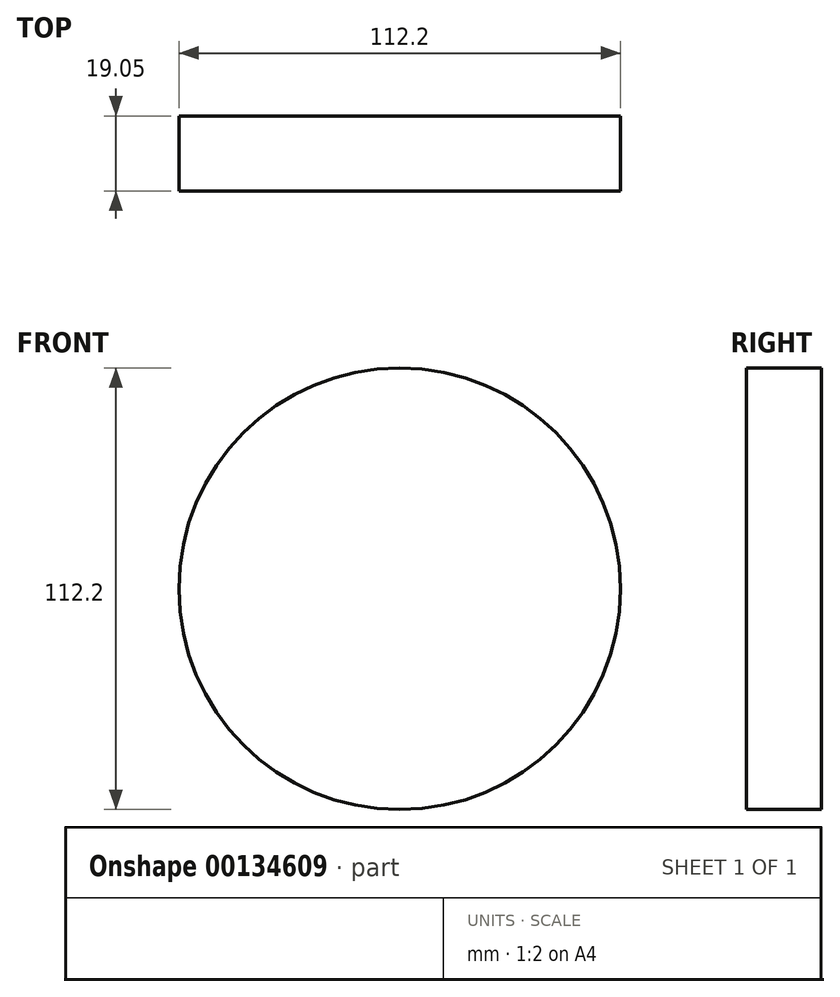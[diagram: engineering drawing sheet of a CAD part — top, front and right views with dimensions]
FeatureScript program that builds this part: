
annotation { "Feature Type Name" : "Feature", "Feature Type Description" : "" }
export const myFeature = defineFeature(function(context is Context, id is Id, definition is map)
    precondition{}
    {
        {
            var Q0;
            Q0=qCreatedBy(makeId("Front.planeOp"),FACE);
            var sketch = newSketch(context, id + "F0", { "sketchPlane" : qUnion([Q0])});
            skCircle(sketch, "E0", {"center": v(0, 0) * mm, "radius": 56.1 * mm});
            skLineSegment(sketch, "E1", {"start": v(-44.78, 33.78) * mm, "end": v(44.83, -33.72) * mm});
            skLineSegment(sketch, "E2", {"start": v(40.5, 38.81) * mm, "end": v(-40.62, -38.69) * mm});
            skText(sketch, "E3", { "text": "J", "fontName": "NotoSansCJKjp-Bold.otf"});
            skText(sketch, "E4", { "text": "H", "fontName": "OpenSans-Bold.ttf"});
            skText(sketch, "E5", { "text": "H", "fontName": "OpenSans-Regular.ttf"});
            skText(sketch, "E6", { "text": "Corp.", "fontName": "OpenSans-Bold.ttf"});
            const initialGuessF0  = {"E3": [-0.01104, 0.02015, 1, 0, 0.02667], "E4": [-0.05098, -0.01186, 1, 0, 0.0266], "E5": [0.02046, -0.01027, 1, 0, 0.02748], "E6": [-0.02794, -0.04342, 1, 0, 0.01773]};
            skSetInitialGuess(sketch, initialGuessF0);
            skSolve(sketch);
        }
        {
            var Q0;
            Q0=makeQuery(id+"F0.imprint","IMPRINT",FACE,{"disambiguationData":[TD([[makeQuery(id+"F0.imprint","IMPRINT",EDGE,{"derivedFrom":sQuery(id+"F0.wireOp",EDGE,"E6.sketch_text.stroke-69")}),-1.0]])]});
            var Q1;
            Q1 = qSketchRegion(id + "F0", true);
            var Q2;
            Q2=makeQuery(id+"F0.imprint","IMPRINT",FACE,{"disambiguationData":[TD([[makeQuery(id+"F0.imprint","IMPRINT",EDGE,{"derivedFrom":sQuery(id+"F0.wireOp",EDGE,"E6.sketch_text.stroke-0")}),1.0]])]});
            var Q3;
            Q3=makeQuery(id+"F0.imprint","IMPRINT",FACE,{"disambiguationData":[TD([[makeQuery(id+"F0.imprint","IMPRINT",EDGE,{"derivedFrom":sQuery(id+"F0.wireOp",EDGE,"E3.sketch_text.stroke-0")}),1.0]])]});
            var Q4;
            Q4=makeQuery(id+"F0.imprint","IMPRINT",FACE,{"disambiguationData":[TD([[makeQuery(id+"F0.imprint","IMPRINT",EDGE,{"derivedFrom":sQuery(id+"F0.wireOp",EDGE,"E4.sketch_text.stroke-0")}),-1.0]])]});
            var Q5;
            Q5=makeQuery(id+"F0.imprint","IMPRINT",FACE,{"disambiguationData":[TD([[makeQuery(id+"F0.imprint","IMPRINT",EDGE,{"derivedFrom":sQuery(id+"F0.wireOp",EDGE,"E5.sketch_text.stroke-0")}),-1.0]])]});
            var Q6;
            Q6=makeQuery(id+"F0.imprint","IMPRINT",FACE,{"disambiguationData":[TD([[makeQuery(id+"F0.imprint","IMPRINT",EDGE,{"derivedFrom":sQuery(id+"F0.wireOp",EDGE,"E6.sketch_text.stroke-0")}),-1.0]])]});
            var Q7;
            Q7=makeQuery(id+"F0.imprint","IMPRINT",FACE,{"disambiguationData":[TD([[makeQuery(id+"F0.imprint","IMPRINT",EDGE,{"derivedFrom":sQuery(id+"F0.wireOp",EDGE,"E6.sketch_text.stroke-15")}),1.0]])]});
            var Q8;
            Q8=makeQuery(id+"F0.imprint","IMPRINT",FACE,{"disambiguationData":[TD([[makeQuery(id+"F0.imprint","IMPRINT",EDGE,{"derivedFrom":sQuery(id+"F0.wireOp",EDGE,"E6.sketch_text.stroke-33")}),-1.0]])]});
            var Q9;
            Q9=makeQuery(id+"F0.imprint","IMPRINT",FACE,{"disambiguationData":[TD([[makeQuery(id+"F0.imprint","IMPRINT",EDGE,{"derivedFrom":sQuery(id+"F0.wireOp",EDGE,"E6.sketch_text.stroke-61")}),1.0]])]});
            var Q10;
            Q10=makeQuery(id+"F0.imprint","IMPRINT",FACE,{"disambiguationData":[TD([[makeQuery(id+"F0.imprint","IMPRINT",EDGE,{"derivedFrom":sQuery(id+"F0.wireOp",EDGE,"E6.sketch_text.stroke-15")}),-1.0]])]});
            var Q11;
            Q11=makeQuery(id+"F0.imprint","IMPRINT",FACE,{"disambiguationData":[TD([[makeQuery(id+"F0.imprint","IMPRINT",EDGE,{"derivedFrom":sQuery(id+"F0.wireOp",EDGE,"E6.sketch_text.stroke-46")}),-1.0]])]});
            var Q12;
            Q12=makeQuery(id+"F0.imprint","IMPRINT",FACE,{"disambiguationData":[TD([[makeQuery(id+"F0.imprint","IMPRINT",EDGE,{"derivedFrom":sQuery(id+"F0.wireOp",EDGE,"E3.sketch_text.stroke-0")}),-1.0]])]});
            var Q13;
            Q13=makeQuery(id+"F0.imprint","IMPRINT",FACE,{"disambiguationData":[TD([[makeQuery(id+"F0.imprint","IMPRINT",EDGE,{"derivedFrom":sQuery(id+"F0.wireOp",EDGE,"E4.sketch_text.stroke-0")}),1.0]])]});
            var Q14;
            Q14=makeQuery(id+"F0.imprint","IMPRINT",FACE,{"disambiguationData":[TD([[makeQuery(id+"F0.imprint","IMPRINT",EDGE,{"derivedFrom":sQuery(id+"F0.wireOp",EDGE,"E5.sketch_text.stroke-0")}),1.0]])]});
            extrude(context, id + "F1", {"entities" : qUnion([Q0, Q1, Q2, Q3, Q4, Q5, Q6, Q7, Q8, Q9, Q10, Q11, Q12, Q13, Q14]), "depth" : 12.7 * mm, "hasSecondDirection" : true, "secondDirectionOppositeDirection" : true, "secondDirectionDepth" : 6.35 * mm});
        }
    });
